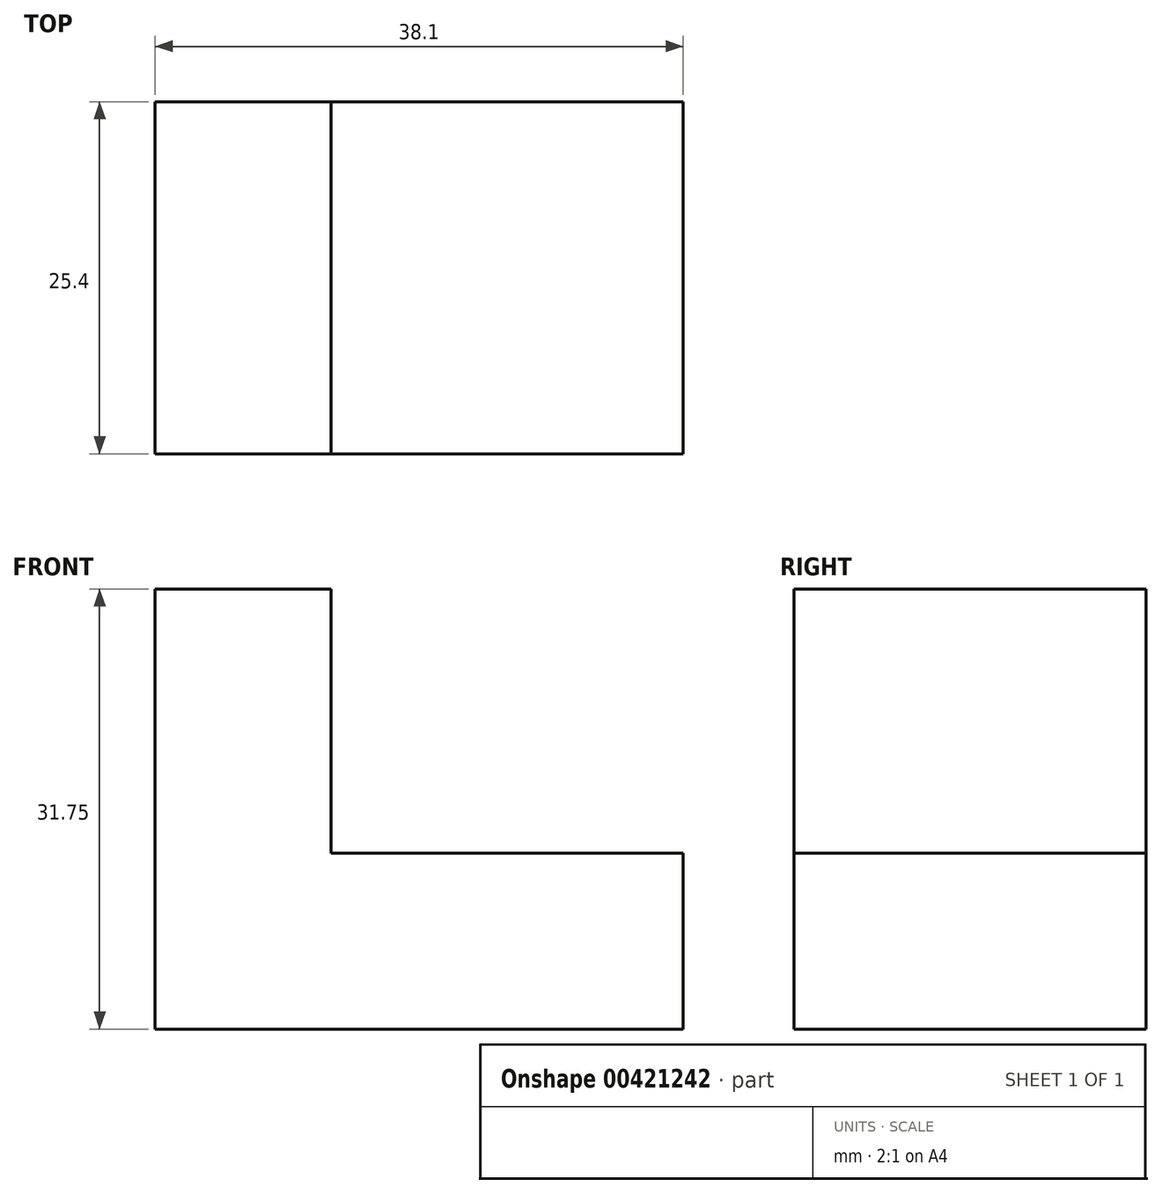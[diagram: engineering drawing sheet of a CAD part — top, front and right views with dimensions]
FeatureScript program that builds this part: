
annotation { "Feature Type Name" : "Feature", "Feature Type Description" : "" }
export const myFeature = defineFeature(function(context is Context, id is Id, definition is map)
    precondition{}
    {
        {
            var Q0;
            Q0=qCreatedBy(makeId("Top.planeOp"),FACE);
            var sketch = newSketch(context, id + "F0", { "sketchPlane" : qUnion([Q0])});
            skLineSegment(sketch, "E0", {"start": v(0, 0) * mm, "end": v(25.4, 0) * mm});
            skLineSegment(sketch, "E1", {"start": v(25.4, 0) * mm, "end": v(25.4, 25.4) * mm});
            skLineSegment(sketch, "E2", {"start": v(25.4, 25.4) * mm, "end": v(0, 25.4) * mm});
            skLineSegment(sketch, "E3", {"start": v(0, 25.4) * mm, "end": v(0, 0) * mm});
            skSolve(sketch);
        }
        {
            var Q0;
            Q0=makeQuery(id+"F0.imprint","IMPRINT",FACE,{"disambiguationData":[TD([[makeQuery(id+"F0.imprint","IMPRINT",EDGE,{"derivedFrom":sQuery(id+"F0.wireOp",EDGE,"E0")}),1.0]])]});
            extrude(context, id + "F1", {"entities" : qUnion([Q0]), "depth" : 12.7 * mm});
        }
        {
            var Q0;
            Q0=qCreatedBy(makeId("Top.planeOp"),FACE);
            var sketch = newSketch(context, id + "F2", { "sketchPlane" : qUnion([Q0])});
            skLineSegment(sketch, "E4", {"start": v(0, 0) * mm, "end": v(-12.7, 0) * mm});
            skLineSegment(sketch, "E5", {"start": v(-12.7, 0) * mm, "end": v(-12.7, 25.4) * mm});
            skLineSegment(sketch, "E6", {"start": v(-12.7, 25.4) * mm, "end": v(0, 25.4) * mm});
            skLineSegment(sketch, "E7", {"start": v(0, 25.4) * mm, "end": v(0, 0) * mm});
            skSolve(sketch);
        }
        {
            var Q0;
            Q0=makeQuery(id+"F2.imprint","IMPRINT",FACE,{"disambiguationData":[TD([[makeQuery(id+"F2.imprint","IMPRINT",EDGE,{"derivedFrom":sQuery(id+"F2.wireOp",EDGE,"E4")}),-1.0]])]});
            extrude(context, id + "F3", {"entities" : qUnion([Q0]), "operationType" : NewBodyOperationType.ADD, "depth" : 31.75 * mm});
        }
    });
